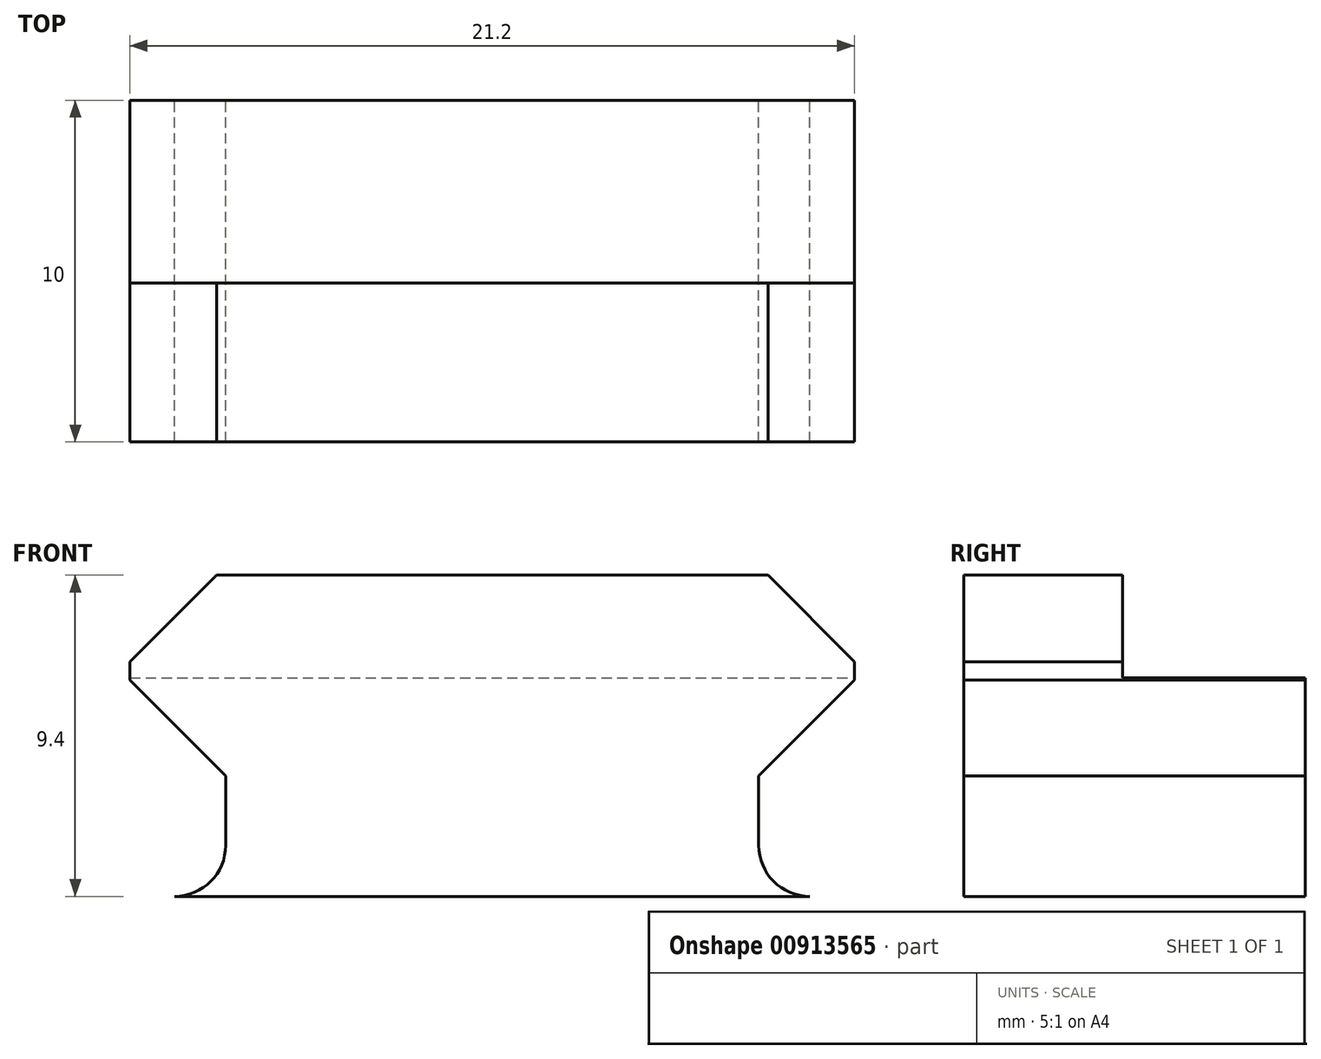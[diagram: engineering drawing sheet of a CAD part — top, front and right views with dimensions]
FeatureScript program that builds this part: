
annotation { "Feature Type Name" : "Feature", "Feature Type Description" : "" }
export const myFeature = defineFeature(function(context is Context, id is Id, definition is map)
    precondition{}
    {
        {
            var Q0;
            Q0=qCreatedBy(makeId("Front.planeOp"),FACE);
            var sketch = newSketch(context, id + "F0", { "sketchPlane" : qUnion([Q0])});
            skLineSegment(sketch, "E0", {"start": v(-10.6, -2.8) * mm, "end": v(10.6, -2.8) * mm, "construction": true});
            skLineSegment(sketch, "E1", {"start": v(-10.6, -3.07) * mm, "end": v(-10.6, -2.53) * mm});
            skLineSegment(sketch, "E2", {"start": v(-10.6, -2.53) * mm, "end": v(-8.07, 0) * mm});
            skLineSegment(sketch, "E3", {"start": v(-8.07, 0) * mm, "end": v(8.07, 0) * mm});
            skLineSegment(sketch, "E4", {"start": v(8.07, 0) * mm, "end": v(10.6, -2.53) * mm});
            skLineSegment(sketch, "E5", {"start": v(10.6, -2.53) * mm, "end": v(10.6, -3.07) * mm});
            skLineSegment(sketch, "E6", {"start": v(10.6, -3.07) * mm, "end": v(7.8, -5.87) * mm});
            skLineSegment(sketch, "E7", {"start": v(7.8, -5.87) * mm, "end": v(7.8, -7.9) * mm});
            skLineSegment(sketch, "E8", {"start": v(-7.8, -7.9) * mm, "end": v(-7.8, -5.87) * mm});
            skLineSegment(sketch, "E9", {"start": v(-7.8, -5.87) * mm, "end": v(-10.6, -3.07) * mm});
            skLineSegment(sketch, "E10", {"start": v(0, 0) * mm, "end": v(0, -9.4) * mm, "construction": true});
            skLineSegment(sketch, "E11", {"start": v(-8.07, 0) * mm, "end": v(-17.76, 0) * mm, "construction": true});
            skLineSegment(sketch, "E12", {"start": v(8.07, 0) * mm, "end": v(18.28, 0) * mm, "construction": true});
            skLineSegment(sketch, "E13", {"start": v(7.8, -9.4) * mm, "end": v(7.8, 0) * mm, "construction": true});
            skLineSegment(sketch, "E14", {"start": v(-9.5, -4.17) * mm, "end": v(9.5, -4.17) * mm, "construction": true});
            skLineSegment(sketch, "E15", {"start": v(9.5, -1.43) * mm, "end": v(-9.5, -1.43) * mm, "construction": true});
            skLineSegment(sketch, "E16", {"start": v(-9.5, -1.43) * mm, "end": v(-9.5, -4.17) * mm, "construction": true});
            skLineSegment(sketch, "E17", {"start": v(9.5, -1.43) * mm, "end": v(9.5, -4.17) * mm, "construction": true});
            skLineSegment(sketch, "E18", {"start": v(9.5, -4.17) * mm, "end": v(9.5, 0) * mm, "construction": true});
            skPoint(sketch, "E19.visualSharp", {"position": v(-7.8, -9.4) * mm});
            skArc(sketch, "E19.filletArc", {"start": v(-9.3, -9.4) * mm, "mid": v(-8.24, -8.96) * mm, "end": v(-7.8, -7.9) * mm});
            skPoint(sketch, "E20.visualSharp", {"position": v(7.8, -9.4) * mm});
            skArc(sketch, "E20.filletArc", {"start": v(7.8, -7.9) * mm, "mid": v(8.24, -8.96) * mm, "end": v(9.3, -9.4) * mm});
            skLineSegment(sketch, "E21", {"start": v(-7.8, -5.87) * mm, "end": v(7.8, -5.87) * mm, "construction": true});
            skLineSegment(sketch, "E22", {"start": v(-9.3, -9.4) * mm, "end": v(9.3, -9.4) * mm});
            skPoint(sketch, "E23", {"position": v(0, -9.4) * mm});
            skSolve(sketch);
        }
        {
            var Q0;
            Q0=qSketchRegion(id+"F0",true);
            extrude(context, id + "F1", {"entities" : qUnion([Q0]), "depth" : 10 * mm});
        }
        {
            var Q0;
            Q0=qCreatedBy(makeId("Front.planeOp"),FACE);
            var sketch = newSketch(context, id + "F2", { "sketchPlane" : qUnion([Q0])});
            skLineSegment(sketch, "E24.bottom", {"start": v(-10.6, 0) * mm, "end": v(10.6, 0) * mm});
            skLineSegment(sketch, "E24.top", {"start": v(-10.6, -3) * mm, "end": v(10.6, -3) * mm});
            skLineSegment(sketch, "E24.left", {"start": v(-10.6, 0) * mm, "end": v(-10.6, -3) * mm});
            skLineSegment(sketch, "E24.right", {"start": v(10.6, 0) * mm, "end": v(10.6, -3) * mm});
            skSolve(sketch);
        }
        {
            var Q0;
            Q0=qSketchRegion(id+"F2",true);
            extrude(context, id + "F3", {"entities" : qUnion([Q0]), "depth" : 5.35 * mm});
        }
        {
            var Q0;
            Q0=makeQuery(id+"F3.opExtrude","SWEPT_BODY",BODY,{"disambiguationData":[OSD([sQuery(id+"F2.wireOp",EDGE,"E24.bottom"),sQuery(id+"F2.wireOp",EDGE,"E24.top"),sQuery(id+"F2.wireOp",EDGE,"E24.left"),sQuery(id+"F2.wireOp",EDGE,"E24.right")])]});
            var Q1;
            Q1=makeQuery(id+"F1.opExtrude","SWEPT_BODY",BODY,{"disambiguationData":[OSD([sQuery(id+"F0.wireOp",EDGE,"E1"),sQuery(id+"F0.wireOp",EDGE,"E2"),sQuery(id+"F0.wireOp",EDGE,"E3"),sQuery(id+"F0.wireOp",EDGE,"E4"),sQuery(id+"F0.wireOp",EDGE,"E5"),sQuery(id+"F0.wireOp",EDGE,"E6"),sQuery(id+"F0.wireOp",EDGE,"E7"),sQuery(id+"F0.wireOp",EDGE,"e10688d7-d44b-45e1-9e71-2647d0456736"),sQuery(id+"F0.wireOp",EDGE,"E8"),sQuery(id+"F0.wireOp",EDGE,"E9"),sQuery(id+"F0.wireOp",EDGE,"2f4cb75b-9706-459d-b0f4-f115e851ccbf"),sQuery(id+"F0.wireOp",EDGE,"df6414be-d73f-43e8-8583-a914b0e8a38a"),sQuery(id+"F0.wireOp",EDGE,"4a54f7f0-58ab-4d26-8cd5-d45017e30607"),sQuery(id+"F0.wireOp",EDGE,"fbdd3cc0-3aed-4f7b-98fb-14e2ed6d7a8c"),sQuery(id+"F0.wireOp",EDGE,"E19.filletArc"),sQuery(id+"F0.wireOp",EDGE,"E20.filletArc")])]});
            booleanBodies(context, id + "F4", {"operationType" : BooleanOperationType.SUBTRACTION, "tools" : qUnion([Q0]), "targets" : qUnion([Q1])});
        }
    });
